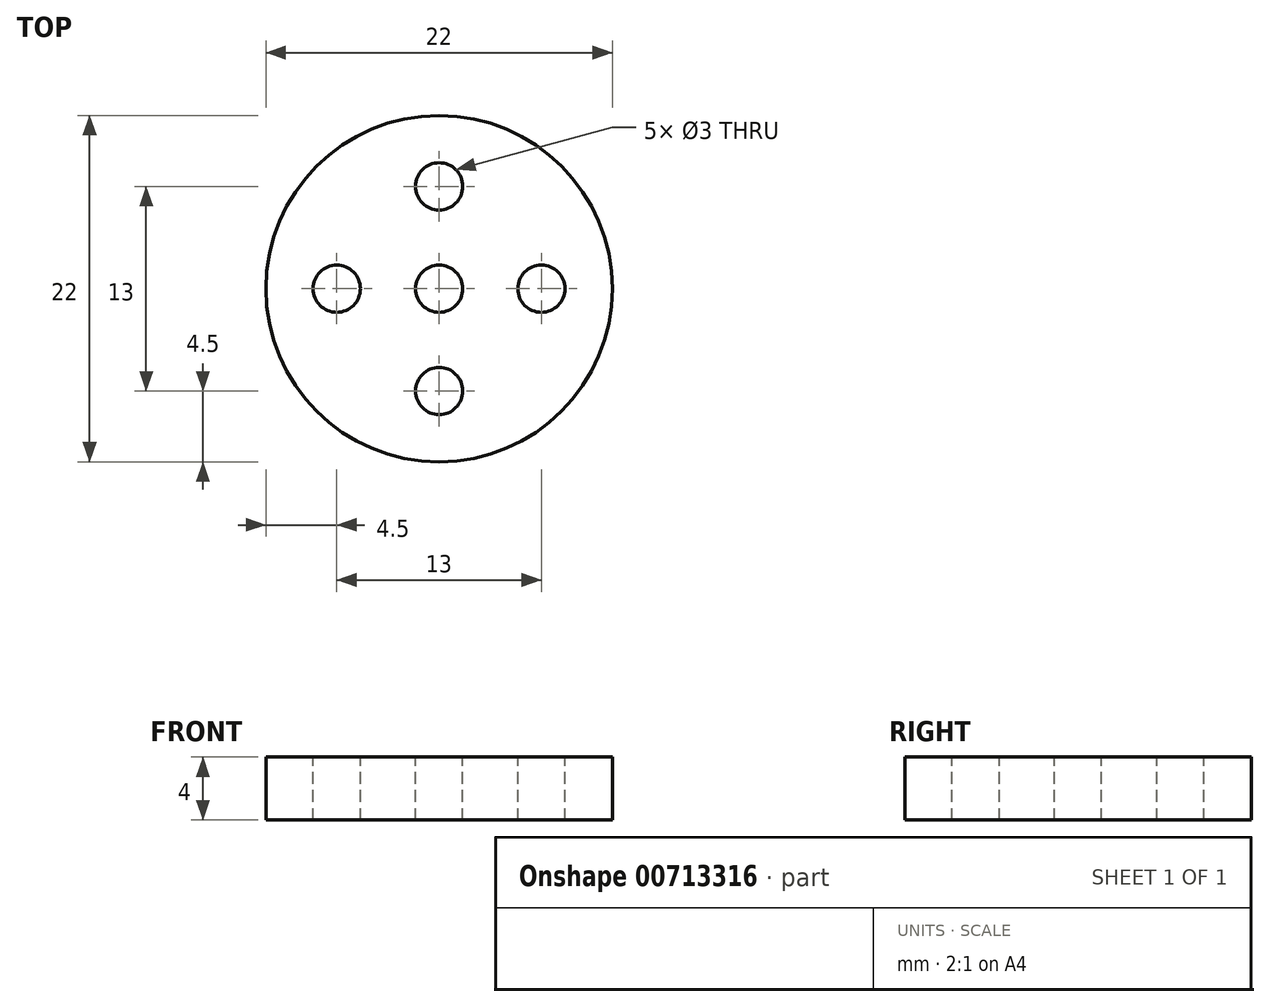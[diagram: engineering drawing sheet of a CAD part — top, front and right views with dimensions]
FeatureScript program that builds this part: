
annotation { "Feature Type Name" : "Feature", "Feature Type Description" : "" }
export const myFeature = defineFeature(function(context is Context, id is Id, definition is map)
    precondition{}
    {
        {
            var Q0;
            Q0=qCreatedBy(makeId("Top.planeOp"),FACE);
            var sketch = newSketch(context, id + "F0", { "sketchPlane" : qUnion([Q0])});
            skCircle(sketch, "E0", {"center": v(0, 0) * mm, "radius": 11 * mm});
            skSolve(sketch);
        }
        {
            var Q0;
            Q0 = qSketchRegion(id + "F0", true);
            extrude(context, id + "F1", {"entities" : qUnion([Q0]), "depth" : 4 * mm, "offsetDistance" : 25 * mm});
        }
        {
            var Q0;
            Q0=makeQuery(id+"F1.opExtrude","CAP_FACE",FACE,{"disambiguationData":[OSD([sQuery(id+"F0.wireOp",EDGE,"E0")])],"isStart":false});
            var sketch = newSketch(context, id + "F2", { "sketchPlane" : qUnion([Q0])});
            skCircle(sketch, "E1", {"center": v(0, 0) * mm, "radius": 1.5 * mm});
            skCircle(sketch, "E2", {"center": v(-6.5, 0) * mm, "radius": 1.5 * mm});
            skCircle(sketch, "E3", {"center": v(0, -6.5) * mm, "radius": 1.5 * mm});
            skCircle(sketch, "E4", {"center": v(6.5, 0) * mm, "radius": 1.5 * mm});
            skCircle(sketch, "E5", {"center": v(0, 6.5) * mm, "radius": 1.5 * mm});
            skSolve(sketch);
        }
        {
            var Q0;
            Q0 = qSketchRegion(id + "F2", true);
            extrude(context, id + "F3", {"entities" : qUnion([Q0]), "operationType" : NewBodyOperationType.REMOVE, "endBound" : BoundingType.THROUGH_ALL, "oppositeDirection" : true, "depth" : 25 * mm, "offsetDistance" : 25 * mm});
        }
    });
